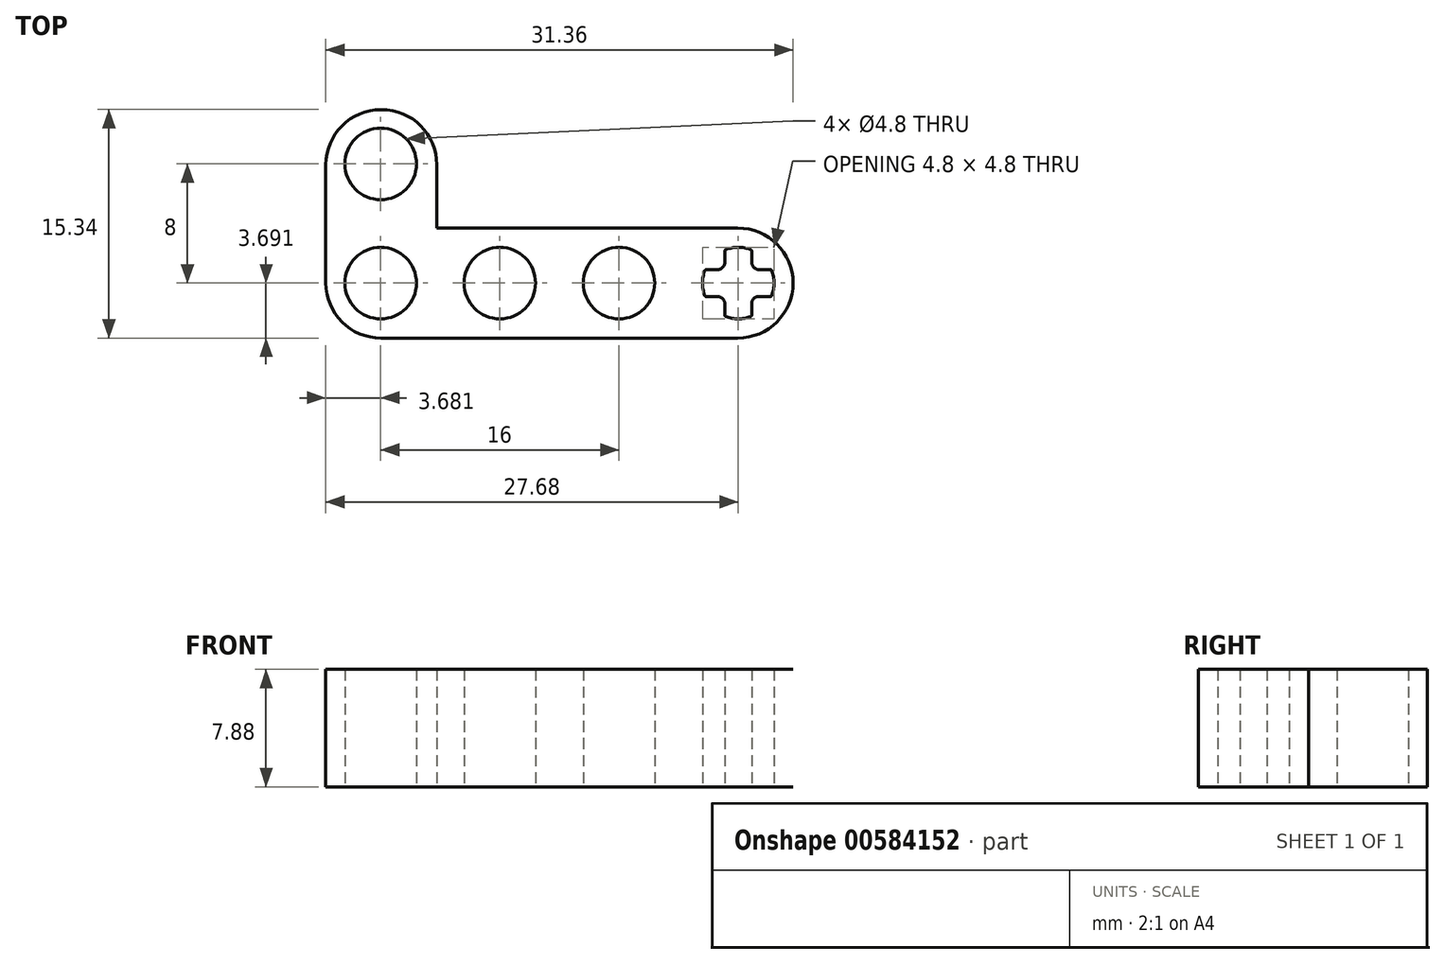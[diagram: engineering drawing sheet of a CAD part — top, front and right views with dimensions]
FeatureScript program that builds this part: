
annotation { "Feature Type Name" : "Feature", "Feature Type Description" : "" }
export const myFeature = defineFeature(function(context is Context, id is Id, definition is map)
    precondition{}
    {
        {
            var Q0;
            Q0=qCreatedBy(makeId("Top.planeOp"),FACE);
            var sketch = newSketch(context, id + "F0", { "sketchPlane" : qUnion([Q0])});
            skLineSegment(sketch, "E0", {"start": v(-28.72, 9.1) * mm, "end": v(-28.72, -19.18) * mm, "construction": true});
            skLineSegment(sketch, "E1", {"start": v(-28.72, -19.18) * mm, "end": v(-29.11, -19.18) * mm, "construction": true});
            skLineSegment(sketch, "E2", {"start": v(-47.58, -2.09) * mm, "end": v(-47.58, -1.54) * mm, "construction": true});
            skLineSegment(sketch, "E3", {"start": v(-28.72, 1.6) * mm, "end": v(-48.4, 1.6) * mm});
            skArc(sketch, "E4", {"start": v(-28.72, 0.31) * mm, "mid": v(-31.12, -2.09) * mm, "end": v(-28.72, -4.49) * mm});
            skCircle(sketch, "E5", {"center": v(-36.72, -2.09) * mm, "radius": 2.4 * mm});
            skCircle(sketch, "E6.1.0.0", {"center": v(-44.72, -2.09) * mm, "radius": 2.4 * mm});
            skLineSegment(sketch, "E7.MirrorCS", {"start": v(-31.32, -5.78) * mm, "end": v(-48.4, -5.78) * mm});
            skArc(sketch, "E8.MirrorCS", {"start": v(-28.72, 0.31) * mm, "mid": v(-26.32, -2.09) * mm, "end": v(-28.72, -4.49) * mm});
            skCircle(sketch, "E9", {"center": v(-44.72, 5.91) * mm, "radius": 2.4 * mm});
            skLineSegment(sketch, "E10", {"start": v(-20.72, 3.2) * mm, "end": v(-20.72, -0.8) * mm, "construction": true});
            skLineSegment(sketch, "E11.0", {"start": v(-21.62, -0.69) * mm, "end": v(-21.62, 0.07) * mm});
            skArc(sketch, "E11.1", {"start": v(-21.62, 0.07) * mm, "mid": v(-21.6, 0.12) * mm, "end": v(-21.55, 0.16) * mm});
            skArc(sketch, "E11.2", {"start": v(-21.55, 0.16) * mm, "mid": v(-20.72, 0.31) * mm, "end": v(-19.88, 0.16) * mm});
            skArc(sketch, "E11.3", {"start": v(-19.88, 0.16) * mm, "mid": v(-19.84, 0.12) * mm, "end": v(-19.82, 0.07) * mm});
            skLineSegment(sketch, "E11.4", {"start": v(-19.82, 0.07) * mm, "end": v(-19.82, -0.69) * mm});
            skArc(sketch, "E11.5", {"start": v(-19.82, -0.69) * mm, "mid": v(-19.67, -1.04) * mm, "end": v(-19.32, -1.19) * mm});
            skLineSegment(sketch, "E11.6", {"start": v(-19.32, -1.19) * mm, "end": v(-18.56, -1.19) * mm});
            skArc(sketch, "E11.7", {"start": v(-22.12, -1.19) * mm, "mid": v(-21.77, -1.04) * mm, "end": v(-21.62, -0.69) * mm});
            skLineSegment(sketch, "E11.8", {"start": v(-22.88, -1.19) * mm, "end": v(-22.12, -1.19) * mm});
            skArc(sketch, "E11.10", {"start": v(-22.97, -1.25) * mm, "mid": v(-22.93, -1.2) * mm, "end": v(-22.88, -1.19) * mm});
            skArc(sketch, "E11.11", {"start": v(-18.56, -1.19) * mm, "mid": v(-18.5, -1.2) * mm, "end": v(-18.47, -1.25) * mm});
            skArc(sketch, "E11.12", {"start": v(-18.47, -1.25) * mm, "mid": v(-18.36, -1.67) * mm, "end": v(-18.32, -2.09) * mm});
            skPoint(sketch, "E12.startSnap0", {"position": v(-23.12, -2.09) * mm});
            skArc(sketch, "E13", {"start": v(-23.12, -2.09) * mm, "mid": v(-23.08, -1.67) * mm, "end": v(-22.97, -1.25) * mm});
            skLineSegment(sketch, "E14", {"start": v(-23.12, -2.09) * mm, "end": v(-18.32, -2.09) * mm, "construction": true});
            skArc(sketch, "E15.MirrorCS", {"start": v(-23.12, -2.09) * mm, "mid": v(-23.08, -2.51) * mm, "end": v(-22.97, -2.92) * mm});
            skArc(sketch, "E16.MirrorCS", {"start": v(-22.97, -2.92) * mm, "mid": v(-22.93, -2.97) * mm, "end": v(-22.88, -2.99) * mm});
            skLineSegment(sketch, "E17.MirrorCS", {"start": v(-22.88, -2.99) * mm, "end": v(-22.12, -2.99) * mm});
            skArc(sketch, "E18.MirrorCS", {"start": v(-22.12, -2.99) * mm, "mid": v(-21.77, -3.14) * mm, "end": v(-21.62, -3.49) * mm});
            skLineSegment(sketch, "E19.MirrorCS", {"start": v(-21.62, -3.49) * mm, "end": v(-21.62, -4.25) * mm});
            skArc(sketch, "E20.MirrorCS", {"start": v(-21.62, -4.25) * mm, "mid": v(-21.6, -4.3) * mm, "end": v(-21.55, -4.34) * mm});
            skArc(sketch, "E21.MirrorCS", {"start": v(-21.55, -4.34) * mm, "mid": v(-20.72, -4.49) * mm, "end": v(-19.88, -4.34) * mm});
            skArc(sketch, "E22.MirrorCS", {"start": v(-19.88, -4.34) * mm, "mid": v(-19.84, -4.3) * mm, "end": v(-19.82, -4.25) * mm});
            skLineSegment(sketch, "E23.MirrorCS", {"start": v(-19.82, -4.25) * mm, "end": v(-19.82, -3.49) * mm});
            skArc(sketch, "E24.MirrorCS", {"start": v(-19.82, -3.49) * mm, "mid": v(-19.67, -3.14) * mm, "end": v(-19.32, -2.99) * mm});
            skLineSegment(sketch, "E25.MirrorCS", {"start": v(-19.32, -2.99) * mm, "end": v(-18.56, -2.99) * mm});
            skArc(sketch, "E26.MirrorCS", {"start": v(-18.56, -2.99) * mm, "mid": v(-18.5, -2.97) * mm, "end": v(-18.47, -2.92) * mm});
            skArc(sketch, "E27.MirrorCS", {"start": v(-18.47, -2.92) * mm, "mid": v(-18.36, -2.51) * mm, "end": v(-18.32, -2.09) * mm});
            skLineSegment(sketch, "E28", {"start": v(-17.04, 1.6) * mm, "end": v(-17.04, -5.78) * mm});
            skLineSegment(sketch, "E29", {"start": v(-36.72, -2.09) * mm, "end": v(-28.72, -2.09) * mm, "construction": true});
            skLineSegment(sketch, "E30", {"start": v(-32.72, 2.75) * mm, "end": v(-32.72, -7.35) * mm, "construction": true});
            skPoint(sketch, "E30.startSnap0", {"position": v(-32.72, -2.09) * mm});
            skLineSegment(sketch, "E31.MirrorCS", {"start": v(-48.4, 1.6) * mm, "end": v(-48.4, -5.78) * mm});
            skLineSegment(sketch, "E32", {"start": v(-48.4, 9.56) * mm, "end": v(-40.95, 9.56) * mm});
            skLineSegment(sketch, "E33", {"start": v(-48.4, 9.56) * mm, "end": v(-48.4, 1.6) * mm});
            skLineSegment(sketch, "E34", {"start": v(-40.95, 9.56) * mm, "end": v(-40.95, 1.6) * mm});
            skLineSegment(sketch, "E35", {"start": v(-28.72, 1.6) * mm, "end": v(-17.04, 1.6) * mm});
            skLineSegment(sketch, "E36", {"start": v(-17.04, -5.78) * mm, "end": v(-31.32, -5.78) * mm});
            skSolve(sketch);
        }
        {
            var Q0;
            Q0=makeQuery(id+"F0.imprint","IMPRINT",FACE,{"disambiguationData":[TD([[makeQuery(id+"F0.imprint","IMPRINT",EDGE,{"derivedFrom":sQuery(id+"F0.wireOp",EDGE,"E3")}),1.0]])]});
            var Q1;
            Q1=makeQuery(id+"F0.imprint","IMPRINT",FACE,{"disambiguationData":[TD([[makeQuery(id+"F0.imprint","IMPRINT",EDGE,{"derivedFrom":sQuery(id+"F0.wireOp",EDGE,"E9")}),-1.0]])]});
            extrude(context, id + "F1", {"entities" : qUnion([Q0, Q1]), "depth" : 7.88 * mm, "offsetDistance" : 25 * mm});
        }
        {
            var Q0;
            Q0=makeQuery(id+"F1.opExtrude","SWEPT_EDGE",EDGE,{"disambiguationData":[OSD([sQuery(id+"F0.wireOp",EDGE,"E32"),sQuery(id+"F0.wireOp",EDGE,"E33")])]});
            var Q1;
            Q1=makeQuery(id+"F1.opExtrude","SWEPT_EDGE",EDGE,{"disambiguationData":[OSD([sQuery(id+"F0.wireOp",EDGE,"E32"),sQuery(id+"F0.wireOp",EDGE,"E34")])]});
            var Q2;
            Q2=makeQuery(id+"F1.opExtrude","SWEPT_EDGE",EDGE,{"disambiguationData":[OSD([sQuery(id+"F0.wireOp",EDGE,"E7.MirrorCS"),sQuery(id+"F0.wireOp",EDGE,"E31.MirrorCS")])]});
            var Q3;
            Q3=makeQuery(id+"F1.opExtrude","SWEPT_EDGE",EDGE,{"disambiguationData":[OSD([sQuery(id+"F0.wireOp",EDGE,"E28"),sQuery(id+"F0.wireOp",EDGE,"E35")])]});
            var Q4;
            Q4=makeQuery(id+"F1.opExtrude","SWEPT_EDGE",EDGE,{"disambiguationData":[OSD([sQuery(id+"F0.wireOp",EDGE,"E28"),sQuery(id+"F0.wireOp",EDGE,"E36")])]});
            fillet(context, id + "F2", {"entities" : qUnion([Q0, Q1, Q2, Q3, Q4]), "radius" : 3.7 * mm, "tangentPropagation" : true, "allowEdgeOverflow" : false});
        }
    });
